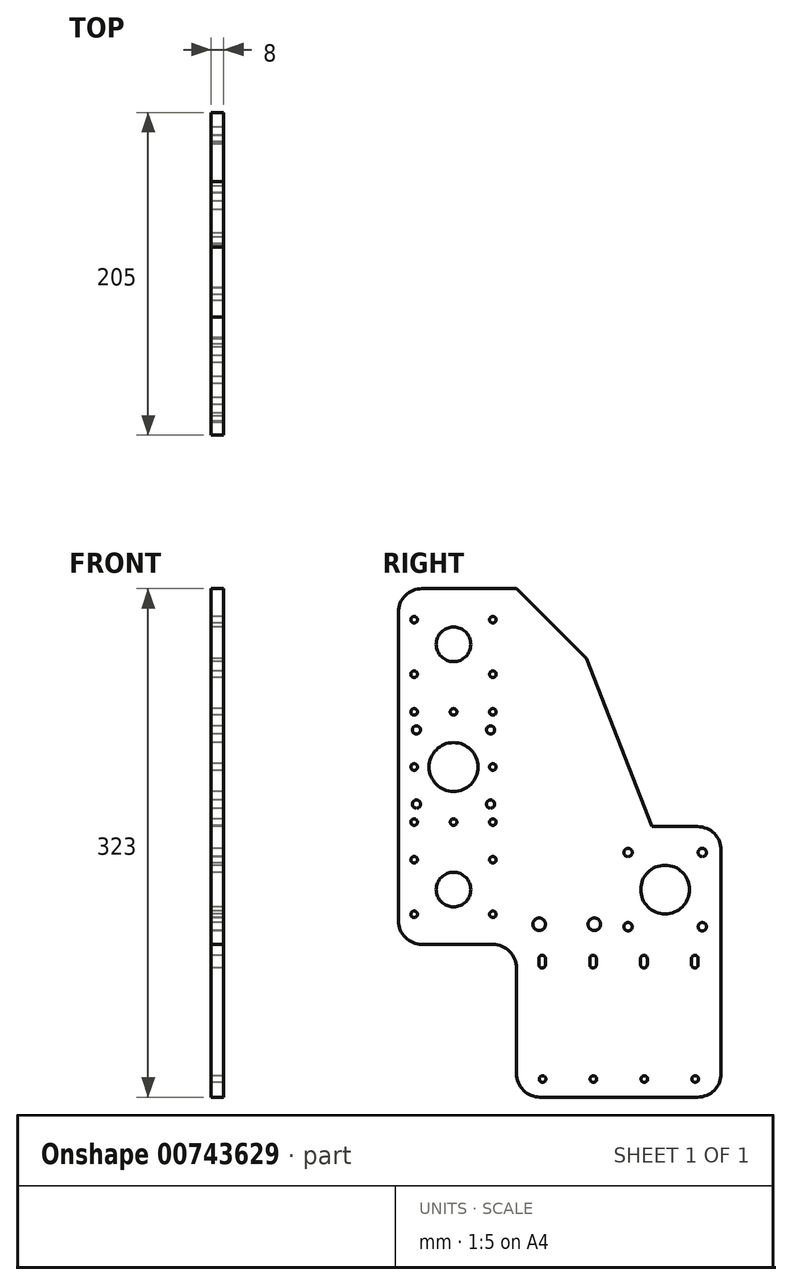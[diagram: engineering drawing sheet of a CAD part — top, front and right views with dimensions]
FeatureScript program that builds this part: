
annotation { "Feature Type Name" : "Feature", "Feature Type Description" : "" }
export const myFeature = defineFeature(function(context is Context, id is Id, definition is map)
    precondition{}
    {
        {
            var Q0;
            Q0=qCreatedBy(makeId("Right.planeOp"),FACE);
            var sketch = newSketch(context, id + "F0", { "sketchPlane" : qUnion([Q0])});
            skLineSegment(sketch, "E0", {"start": v(15, -20) * mm, "end": v(115, -20) * mm});
            skLineSegment(sketch, "E1", {"start": v(130, -5) * mm, "end": v(130, 136.83) * mm});
            skLineSegment(sketch, "E2", {"start": v(115, 151.83) * mm, "end": v(85.92, 151.83) * mm});
            skLineSegment(sketch, "E3", {"start": v(85.92, 151.83) * mm, "end": v(44.49, 258.51) * mm});
            skLineSegment(sketch, "E4", {"start": v(44.49, 258.51) * mm, "end": v(0, 303) * mm});
            skLineSegment(sketch, "E5", {"start": v(0, 303) * mm, "end": v(-60, 303) * mm});
            skLineSegment(sketch, "E6", {"start": v(-75, 288) * mm, "end": v(-75, 92) * mm});
            skLineSegment(sketch, "E7", {"start": v(-60, 77) * mm, "end": v(-15, 77) * mm});
            skLineSegment(sketch, "E8", {"start": v(0, 62) * mm, "end": v(0, -5) * mm});
            skCircle(sketch, "E9", {"center": v(16.54, -8.5) * mm, "radius": 2.1 * mm});
            skCircle(sketch, "E10.1.0.0", {"center": v(48.86, -8.5) * mm, "radius": 2.1 * mm});
            skCircle(sketch, "E10.2.0.0", {"center": v(81.18, -8.5) * mm, "radius": 2.1 * mm});
            skCircle(sketch, "E10.3.0.0", {"center": v(113.5, -8.5) * mm, "radius": 2.1 * mm});
            skLineSegment(sketch, "E10.direction1", {"start": v(16.54, -8.5) * mm, "end": v(48.86, -8.5) * mm, "construction": true});
            skLineSegment(sketch, "E11", {"start": v(16.29, 68.08) * mm, "end": v(16.29, 64.08) * mm});
            skArc(sketch, "E12.0.startCap", {"start": v(14.19, 68.08) * mm, "mid": v(16.29, 70.18) * mm, "end": v(18.39, 68.08) * mm});
            skArc(sketch, "E12.0.endCap", {"start": v(18.39, 64.08) * mm, "mid": v(16.29, 61.98) * mm, "end": v(14.19, 64.08) * mm});
            skLineSegment(sketch, "E12.0.left", {"start": v(18.39, 68.08) * mm, "end": v(18.39, 64.08) * mm});
            skLineSegment(sketch, "E12.0.right", {"start": v(14.19, 68.08) * mm, "end": v(14.19, 64.08) * mm});
            skArc(sketch, "E13.1.0.0", {"start": v(46.5, 68.08) * mm, "mid": v(48.6, 70.18) * mm, "end": v(50.7, 68.08) * mm});
            skLineSegment(sketch, "E13.1.0.1", {"start": v(48.6, 68.08) * mm, "end": v(48.6, 64.08) * mm});
            skLineSegment(sketch, "E13.1.0.2", {"start": v(50.7, 68.08) * mm, "end": v(50.7, 64.08) * mm});
            skLineSegment(sketch, "E13.1.0.3", {"start": v(46.5, 68.08) * mm, "end": v(46.5, 64.08) * mm});
            skArc(sketch, "E13.1.0.4", {"start": v(50.7, 64.08) * mm, "mid": v(48.6, 61.98) * mm, "end": v(46.5, 64.08) * mm});
            skArc(sketch, "E13.2.0.0", {"start": v(78.83, 68.08) * mm, "mid": v(80.93, 70.18) * mm, "end": v(83.03, 68.08) * mm});
            skLineSegment(sketch, "E13.2.0.1", {"start": v(80.93, 68.08) * mm, "end": v(80.93, 64.08) * mm});
            skLineSegment(sketch, "E13.2.0.2", {"start": v(83.03, 68.08) * mm, "end": v(83.03, 64.08) * mm});
            skLineSegment(sketch, "E13.2.0.3", {"start": v(78.83, 68.08) * mm, "end": v(78.83, 64.08) * mm});
            skArc(sketch, "E13.2.0.4", {"start": v(83.03, 64.08) * mm, "mid": v(80.93, 61.98) * mm, "end": v(78.83, 64.08) * mm});
            skArc(sketch, "E13.3.0.0", {"start": v(111.15, 68.08) * mm, "mid": v(113.25, 70.18) * mm, "end": v(115.35, 68.08) * mm});
            skLineSegment(sketch, "E13.3.0.1", {"start": v(113.25, 68.08) * mm, "end": v(113.25, 64.08) * mm});
            skLineSegment(sketch, "E13.3.0.2", {"start": v(115.35, 68.08) * mm, "end": v(115.35, 64.08) * mm});
            skLineSegment(sketch, "E13.3.0.3", {"start": v(111.15, 68.08) * mm, "end": v(111.15, 64.08) * mm});
            skArc(sketch, "E13.3.0.4", {"start": v(115.35, 64.08) * mm, "mid": v(113.25, 61.98) * mm, "end": v(111.15, 64.08) * mm});
            skLineSegment(sketch, "E13.direction1", {"start": v(14.19, 64.08) * mm, "end": v(46.5, 64.08) * mm, "construction": true});
            skLineSegment(sketch, "E14", {"start": v(-51.84, 0) * mm, "end": v(156.45, 0) * mm, "construction": true});
            skCircle(sketch, "E15", {"center": v(118, 135.4) * mm, "radius": 2.65 * mm});
            skCircle(sketch, "E16", {"center": v(94.43, 111.83) * mm, "radius": 15.5 * mm});
            skCircle(sketch, "E17", {"center": v(70.86, 88.26) * mm, "radius": 2.65 * mm});
            skCircle(sketch, "E18", {"center": v(70.86, 135.4) * mm, "radius": 2.65 * mm});
            skCircle(sketch, "E19", {"center": v(118, 88.26) * mm, "radius": 2.65 * mm});
            skCircle(sketch, "E20", {"center": v(49.43, 89.83) * mm, "radius": 4 * mm});
            skCircle(sketch, "E21", {"center": v(14.43, 89.83) * mm, "radius": 4 * mm});
            skCircle(sketch, "E22", {"center": v(-40, 111.83) * mm, "radius": 11 * mm});
            skCircle(sketch, "E23", {"center": v(-40, 189.72) * mm, "radius": 15.5 * mm});
            skCircle(sketch, "E24", {"center": v(-40, 267.6) * mm, "radius": 11 * mm});
            skCircle(sketch, "E25", {"center": v(-65, 96.14) * mm, "radius": 2.1 * mm});
            skCircle(sketch, "E26", {"center": v(-15, 96.14) * mm, "radius": 2.1 * mm});
            skCircle(sketch, "E27", {"center": v(-15, 130.8) * mm, "radius": 2.1 * mm});
            skCircle(sketch, "E28", {"center": v(-65, 130.8) * mm, "radius": 2.1 * mm});
            skCircle(sketch, "E29", {"center": v(-65, 283.3) * mm, "radius": 2.1 * mm});
            skCircle(sketch, "E30", {"center": v(-15, 283.3) * mm, "radius": 2.1 * mm});
            skCircle(sketch, "E31", {"center": v(-15, 248.64) * mm, "radius": 2.1 * mm});
            skCircle(sketch, "E32", {"center": v(-65, 248.64) * mm, "radius": 2.1 * mm});
            skCircle(sketch, "E33", {"center": v(-65, 224.72) * mm, "radius": 2.1 * mm});
            skCircle(sketch, "E34", {"center": v(-15, 224.72) * mm, "radius": 2.1 * mm});
            skCircle(sketch, "E35", {"center": v(-15, 154.72) * mm, "radius": 2.1 * mm});
            skCircle(sketch, "E36", {"center": v(-65, 154.72) * mm, "radius": 2.1 * mm});
            skCircle(sketch, "E37", {"center": v(-63.57, 166.15) * mm, "radius": 2.6 * mm});
            skCircle(sketch, "E38", {"center": v(-16.43, 166.15) * mm, "radius": 2.6 * mm});
            skCircle(sketch, "E39", {"center": v(-16.43, 213.3) * mm, "radius": 2.6 * mm});
            skCircle(sketch, "E40", {"center": v(-63.57, 213.3) * mm, "radius": 2.6 * mm});
            skPoint(sketch, "E41.visualSharp", {"position": v(-75, 303) * mm});
            skArc(sketch, "E41.filletArc", {"start": v(-60, 303) * mm, "mid": v(-70.6, 298.6) * mm, "end": v(-75, 288) * mm});
            skPoint(sketch, "E42.visualSharp", {"position": v(-75, 77) * mm});
            skArc(sketch, "E42.filletArc", {"start": v(-75, 92) * mm, "mid": v(-70.6, 81.4) * mm, "end": v(-60, 77) * mm});
            skPoint(sketch, "E43.visualSharp", {"position": v(0, 77) * mm});
            skArc(sketch, "E43.filletArc", {"start": v(0, 62) * mm, "mid": v(-4.4, 72.6) * mm, "end": v(-15, 77) * mm});
            skPoint(sketch, "E44.visualSharp", {"position": v(0, -20) * mm});
            skArc(sketch, "E44.filletArc", {"start": v(0, -5) * mm, "mid": v(4.4, -15.6) * mm, "end": v(15, -20) * mm});
            skPoint(sketch, "E45.visualSharp", {"position": v(130, -20) * mm});
            skArc(sketch, "E45.filletArc", {"start": v(115, -20) * mm, "mid": v(125.6, -15.6) * mm, "end": v(130, -5) * mm});
            skPoint(sketch, "E46.visualSharp", {"position": v(130, 151.83) * mm});
            skArc(sketch, "E46.filletArc", {"start": v(130, 136.83) * mm, "mid": v(125.6, 147.44) * mm, "end": v(115, 151.83) * mm});
            skCircle(sketch, "E47", {"center": v(-15, 189.72) * mm, "radius": 2.1 * mm});
            skCircle(sketch, "E48", {"center": v(-65, 189.72) * mm, "radius": 2.1 * mm});
            skCircle(sketch, "E49", {"center": v(-40, 224.72) * mm, "radius": 2.1 * mm});
            skCircle(sketch, "E50", {"center": v(-40, 154.72) * mm, "radius": 2.1 * mm});
            skSolve(sketch);
        }
        {
            var Q0;
            Q0=makeQuery(id+"F0.imprint","IMPRINT",FACE,{"disambiguationData":[TD([[makeQuery(id+"F0.imprint","IMPRINT",EDGE,{"derivedFrom":sQuery(id+"F0.wireOp",EDGE,"E0")}),1.0]])]});
            extrude(context, id + "F1", {"entities" : qUnion([Q0]), "depth" : 8 * mm, "offsetDistance" : 25 * mm});
        }
    });
